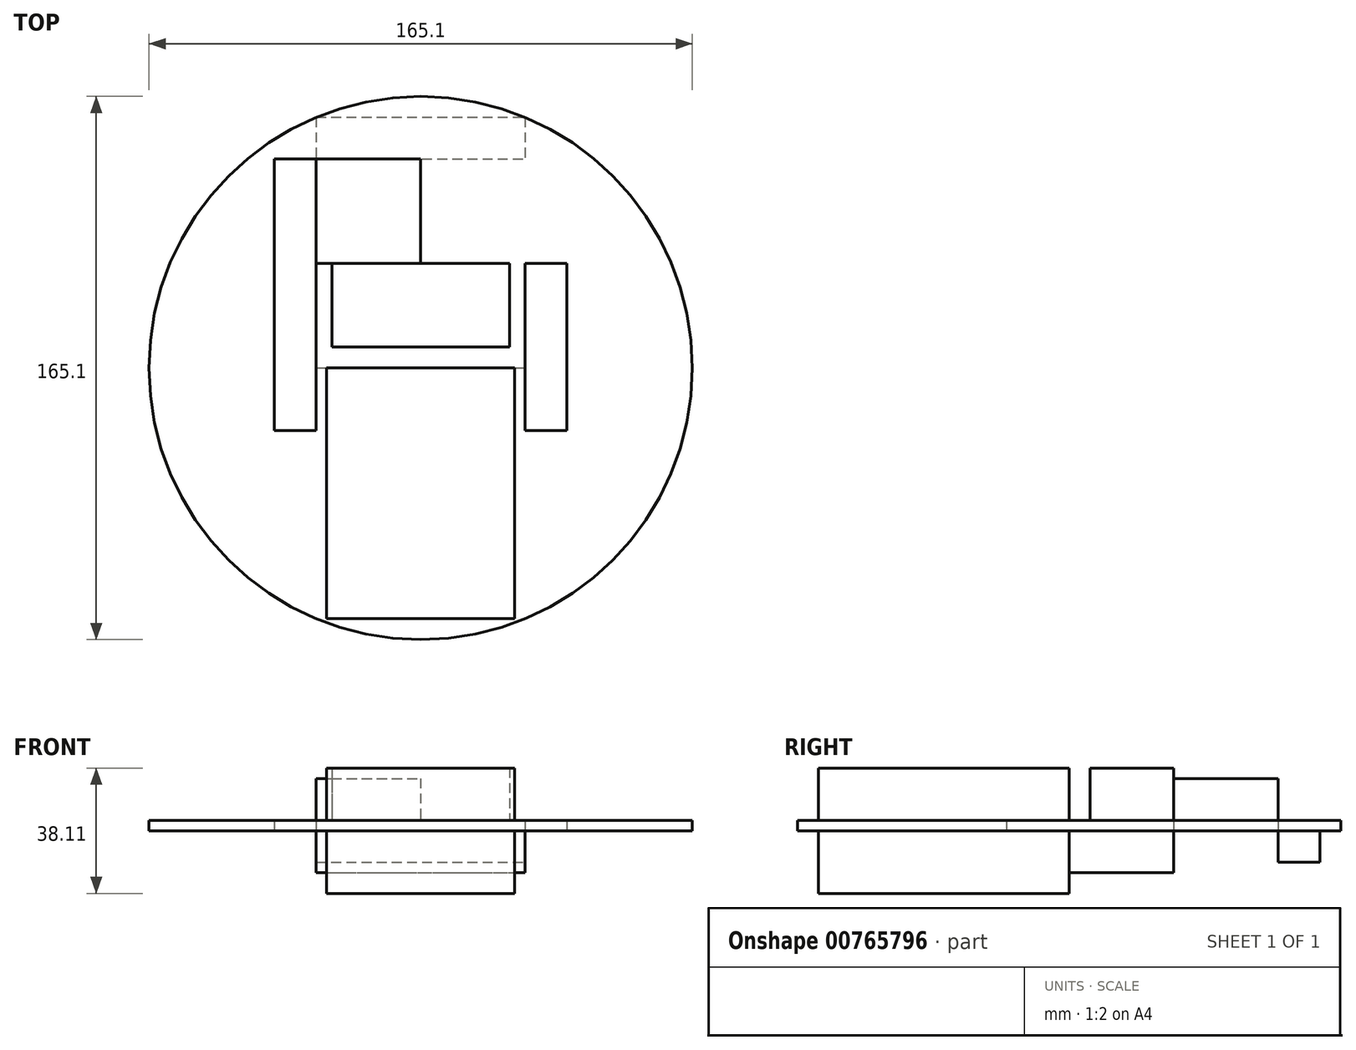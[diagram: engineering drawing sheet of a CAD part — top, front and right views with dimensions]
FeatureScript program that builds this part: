
annotation { "Feature Type Name" : "Feature", "Feature Type Description" : "" }
export const myFeature = defineFeature(function(context is Context, id is Id, definition is map)
    precondition{}
    {
        {
            var Q0;
            Q0=qCreatedBy(makeId("Top.planeOp"),FACE);
            var sketch = newSketch(context, id + "F0", { "sketchPlane" : qUnion([Q0])});
            skCircle(sketch, "E0", {"center": v(0, 0) * mm, "radius": 82.55 * mm});
            skLineSegment(sketch, "E1", {"start": v(0, 82.55) * mm, "end": v(0, 0) * mm, "construction": true});
            skLineSegment(sketch, "E2", {"start": v(-82.55, 0) * mm, "end": v(0, 0) * mm, "construction": true});
            skLineSegment(sketch, "E3", {"start": v(0, 0) * mm, "end": v(0, -82.55) * mm, "construction": true});
            skLineSegment(sketch, "E4", {"start": v(0, 0) * mm, "end": v(82.55, 0) * mm, "construction": true});
            skLineSegment(sketch, "E5", {"start": v(-41.28, 0) * mm, "end": v(-41.28, 71.5) * mm, "construction": true});
            skLineSegment(sketch, "E6", {"start": v(-41.28, 0) * mm, "end": v(-41.28, -71.5) * mm, "construction": true});
            skLineSegment(sketch, "E7", {"start": v(41.28, -71.5) * mm, "end": v(41.28, 71.5) * mm, "construction": true});
            skPoint(sketch, "E7.startSnap0", {"position": v(41.28, 0) * mm});
            skLineSegment(sketch, "E8", {"start": v(71.5, 41.28) * mm, "end": v(-71.5, 41.28) * mm, "construction": true});
            skPoint(sketch, "E8.startSnap0", {"position": v(0, 41.28) * mm});
            skLineSegment(sketch, "E9", {"start": v(71.5, -41.28) * mm, "end": v(-71.5, -41.28) * mm, "construction": true});
            skPoint(sketch, "E9.startSnap0", {"position": v(0, -41.28) * mm});
            skSolve(sketch);
        }
        {
            var Q0;
            Q0=qCreatedBy(makeId("Top.planeOp"),FACE);
            var sketch = newSketch(context, id + "F1", { "sketchPlane" : qUnion([Q0])});
            skLineSegment(sketch, "E10.bottom", {"start": v(-31.75, 63.5) * mm, "end": v(31.75, 63.5) * mm});
            skLineSegment(sketch, "E10.top", {"start": v(-31.75, 76.2) * mm, "end": v(31.75, 76.2) * mm});
            skLineSegment(sketch, "E10.left", {"start": v(-31.75, 76.2) * mm, "end": v(-31.75, 63.5) * mm});
            skLineSegment(sketch, "E10.right", {"start": v(31.75, 76.2) * mm, "end": v(31.75, 63.5) * mm});
            skPoint(sketch, "E11", {"position": v(0, 76.2) * mm});
            skLineSegment(sketch, "E12.bottom", {"start": v(-28.58, 0) * mm, "end": v(28.58, 0) * mm});
            skLineSegment(sketch, "E12.top", {"start": v(-28.58, -76.2) * mm, "end": v(28.58, -76.2) * mm});
            skLineSegment(sketch, "E12.left", {"start": v(-28.58, 0) * mm, "end": v(-28.58, -76.2) * mm});
            skLineSegment(sketch, "E12.right", {"start": v(28.58, 0) * mm, "end": v(28.57, -76.2) * mm});
            skLineSegment(sketch, "E13.bottom", {"start": v(-26.99, 31.75) * mm, "end": v(26.99, 31.75) * mm});
            skLineSegment(sketch, "E13.top", {"start": v(-26.99, 6.35) * mm, "end": v(26.99, 6.35) * mm});
            skLineSegment(sketch, "E13.left", {"start": v(-26.99, 31.75) * mm, "end": v(-26.99, 6.35) * mm});
            skLineSegment(sketch, "E13.right", {"start": v(26.99, 31.75) * mm, "end": v(26.99, 6.35) * mm});
            skLineSegment(sketch, "E14.bottom", {"start": v(-31.75, 63.5) * mm, "end": v(0, 63.5) * mm});
            skLineSegment(sketch, "E14.top", {"start": v(-31.75, 31.75) * mm, "end": v(0, 31.75) * mm});
            skLineSegment(sketch, "E14.left", {"start": v(-31.75, 63.5) * mm, "end": v(-31.75, 31.75) * mm});
            skLineSegment(sketch, "E14.right", {"start": v(0, 63.5) * mm, "end": v(0, 31.75) * mm});
            skPoint(sketch, "E15", {"position": v(0, 31.75) * mm});
            skPoint(sketch, "E16", {"position": v(0, 0) * mm});
            skSolve(sketch);
        }
        {
            var Q0;
            Q0 = qSketchRegion(id + "F0", true);
            extrude(context, id + "F2", {"entities" : qUnion([Q0]), "oppositeDirection" : true, "depth" : 3.17 * mm, "offsetDistance" : 25.4 * mm});
        }
        {
            var Q0;
            Q0=makeQuery(id+"F1.imprint","IMPRINT",FACE,{"disambiguationData":[TD([[makeQuery(id+"F1.imprint","IMPRINT",EDGE,{"derivedFrom":sQuery(id+"F1.wireOp",EDGE,"E12.bottom")}),-1.0]])]});
            extrude(context, id + "F3", {"entities" : qUnion([Q0]), "operationType" : NewBodyOperationType.ADD, "depth" : 15.88 * mm, "offsetDistance" : 25.4 * mm});
        }
        {
            var Q0;
            Q0=makeQuery(id+"F1.imprint","IMPRINT",FACE,{"disambiguationData":[TD([[makeQuery(id+"F1.imprint","IMPRINT",EDGE,{"derivedFrom":sQuery(id+"F1.wireOp",EDGE,"E12.bottom")}),-1.0]])]});
            extrude(context, id + "F4", {"entities" : qUnion([Q0]), "operationType" : NewBodyOperationType.ADD, "oppositeDirection" : true, "depth" : 22.22 * mm, "offsetDistance" : 25.4 * mm});
        }
        {
            var Q0;
            Q0=makeQuery(id+"F1.imprint","IMPRINT",FACE,{"disambiguationData":[TD([[makeQuery(id+"F1.imprint","IMPRINT",EDGE,{"derivedFrom":sQuery(id+"F1.wireOp",EDGE,"E10.top")}),-1.0]])]});
            extrude(context, id + "F5", {"entities" : qUnion([Q0]), "operationType" : NewBodyOperationType.ADD, "oppositeDirection" : true, "depth" : 12.7 * mm, "offsetDistance" : 25.4 * mm});
        }
        {
            var Q0;
            {var subQ0=sQuery(id+"F1.wireOp",EDGE,"E14.top");Q0=makeQuery(id+"F1.imprint","IMPRINT",FACE,{"disambiguationData":[TD([[makeQuery(id+"F1.imprint","IMPRINT",EDGE,{"derivedFrom":subQ0}),1.0]])]});}
            extrude(context, id + "F6", {"entities" : qUnion([Q0]), "operationType" : NewBodyOperationType.ADD, "depth" : 12.7 * mm, "offsetDistance" : 25.4 * mm});
        }
        {
            var Q0;
            Q0=makeQuery(id+"F1.imprint","IMPRINT",FACE,{"disambiguationData":[TD([[makeQuery(id+"F1.imprint","IMPRINT",EDGE,{"derivedFrom":sQuery(id+"F1.wireOp",EDGE,"E13.top")}),1.0]])]});
            extrude(context, id + "F7", {"entities" : qUnion([Q0]), "operationType" : NewBodyOperationType.ADD, "depth" : 15.88 * mm, "offsetDistance" : 25.4 * mm});
        }
        {
            var Q0;
            {var subQ0=sQuery(id+"F0.wireOp",EDGE,"E0");var subQ1=makeQuery(id+"F2.opExtrude","CAP_FACE",FACE,{"disambiguationData":[OSD([subQ0])],"isStart":false});Q0=makeQuery(id+"F5.boolean.opBoolean","SPLIT",FACE,{"disambiguationData":[TD([makeQuery(id+"F2.opExtrude","SWEPT_FACE",FACE,{"disambiguationData":[OSD([subQ0])]}),subQ1,makeQuery(id+"F4.opExtrude","SWEPT_FACE",FACE,{"disambiguationData":[OSD([sQuery(id+"F1.wireOp",EDGE,"E12.bottom")])]}),makeQuery(id+"F4.opExtrude","SWEPT_FACE",FACE,{"disambiguationData":[OSD([sQuery(id+"F1.wireOp",EDGE,"E12.top")])]}),makeQuery(id+"F4.opExtrude","SWEPT_FACE",FACE,{"disambiguationData":[OSD([sQuery(id+"F1.wireOp",EDGE,"E12.left")])]}),makeQuery(id+"F4.opExtrude","SWEPT_FACE",FACE,{"disambiguationData":[OSD([sQuery(id+"F1.wireOp",EDGE,"E12.right")])]}),makeQuery(id+"F5.opExtrude","SWEPT_FACE",FACE,{"disambiguationData":[OSD([sQuery(id+"F1.wireOp",EDGE,"E10.bottom")])]}),makeQuery(id+"F5.opExtrude","SWEPT_FACE",FACE,{"disambiguationData":[OSD([sQuery(id+"F1.wireOp",EDGE,"E10.top")])]}),makeQuery(id+"F5.opExtrude","SWEPT_FACE",FACE,{"disambiguationData":[OSD([sQuery(id+"F1.wireOp",EDGE,"E10.left")])]}),makeQuery(id+"F5.opExtrude","SWEPT_FACE",FACE,{"disambiguationData":[OSD([sQuery(id+"F1.wireOp",EDGE,"E10.right")])]})])],"derivedFrom":subQ1});}
            var sketch = newSketch(context, id + "F8", { "sketchPlane" : qUnion([Q0])});
            skLineSegment(sketch, "E17.bottom", {"start": v(-31.75, 0) * mm, "end": v(31.75, 0) * mm});
            skLineSegment(sketch, "E17.top", {"start": v(-31.75, -31.75) * mm, "end": v(31.75, -31.75) * mm});
            skLineSegment(sketch, "E17.left", {"start": v(-31.75, 0) * mm, "end": v(-31.75, -31.75) * mm});
            skLineSegment(sketch, "E17.right", {"start": v(31.75, 0) * mm, "end": v(31.75, -31.75) * mm});
            skPoint(sketch, "E18", {"position": v(0, 0) * mm});
            skLineSegment(sketch, "E19.bottom", {"start": v(-44.45, 19.05) * mm, "end": v(-31.75, 19.05) * mm});
            skLineSegment(sketch, "E19.top", {"start": v(-44.45, -63.5) * mm, "end": v(-31.75, -63.5) * mm});
            skLineSegment(sketch, "E19.left", {"start": v(-44.45, 19.05) * mm, "end": v(-44.45, -63.5) * mm});
            skLineSegment(sketch, "E19.right", {"start": v(-31.75, 19.05) * mm, "end": v(-31.75, -63.5) * mm});
            skLineSegment(sketch, "E20.bottom", {"start": v(31.75, 19.05) * mm, "end": v(44.45, 19.05) * mm});
            skLineSegment(sketch, "E20.top", {"start": v(31.75, -31.75) * mm, "end": v(44.45, -31.75) * mm});
            skLineSegment(sketch, "E20.left", {"start": v(31.75, 19.05) * mm, "end": v(31.75, -31.75) * mm});
            skLineSegment(sketch, "E20.right", {"start": v(44.45, 19.05) * mm, "end": v(44.45, -31.75) * mm});
            skSolve(sketch);
        }
        {
            var Q0;
            Q0=makeQuery(id+"F8.imprint","IMPRINT",FACE,{"disambiguationData":[TD([[makeQuery(id+"F8.imprint","IMPRINT",EDGE,{"derivedFrom":sQuery(id+"F8.wireOp",EDGE,"E17.top")}),1.0]])]});
            extrude(context, id + "F9", {"entities" : qUnion([Q0]), "operationType" : NewBodyOperationType.ADD, "depth" : 12.7 * mm, "offsetDistance" : 25.4 * mm});
        }
        {
            var Q0;
            {var subQ3=sQuery(id+"F8.wireOp",EDGE,"E20.bottom");Q0=makeQuery(id+"F8.imprint","IMPRINT",FACE,{"disambiguationData":[TD([[makeQuery(id+"F8.imprint","IMPRINT",EDGE,{"derivedFrom":subQ3}),-1.0]])]});}
            var Q1;
            {var subQ2=sQuery(id+"F8.wireOp",EDGE,"E19.bottom");Q1=makeQuery(id+"F8.imprint","IMPRINT",FACE,{"disambiguationData":[TD([[makeQuery(id+"F8.imprint","IMPRINT",EDGE,{"derivedFrom":subQ2}),-1.0]])]});}
            extrude(context, id + "F10", {"entities" : qUnion([Q0, Q1]), "operationType" : NewBodyOperationType.REMOVE, "oppositeDirection" : true, "depth" : 25.4 * mm, "offsetDistance" : 25.4 * mm});
        }
    });
